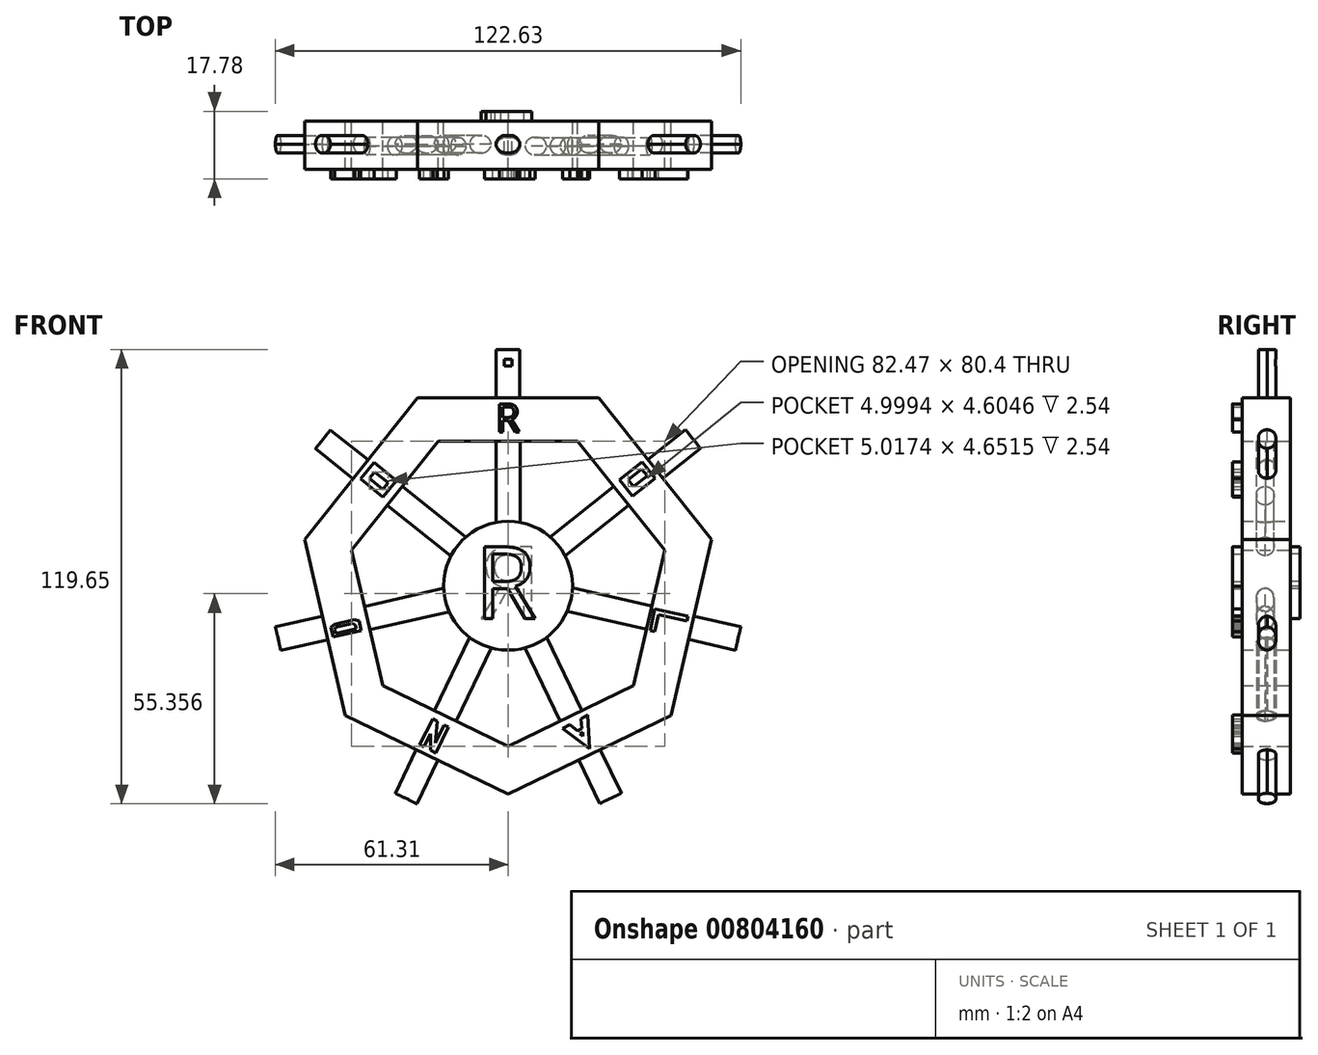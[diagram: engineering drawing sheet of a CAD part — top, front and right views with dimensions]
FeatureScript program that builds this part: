
annotation { "Feature Type Name" : "Feature", "Feature Type Description" : "" }
export const myFeature = defineFeature(function(context is Context, id is Id, definition is map)
    precondition{}
    {
        {
            var Q0;
            Q0=qCreatedBy(makeId("Front.planeOp"),FACE);
            var sketch = newSketch(context, id + "F0", { "sketchPlane" : qUnion([Q0])});
            skCircle(sketch, "E0.cCircle", {"center": v(0, 0) * mm, "radius": 49.5 * mm, "construction": true});
            skLineSegment(sketch, "E0.0", {"start": v(-23.84, 49.5) * mm, "end": v(23.84, 49.5) * mm});
            skLineSegment(sketch, "E0.1", {"start": v(23.84, 49.5) * mm, "end": v(53.56, 12.22) * mm});
            skLineSegment(sketch, "E0.2", {"start": v(53.56, 12.22) * mm, "end": v(42.95, -34.25) * mm});
            skLineSegment(sketch, "E0.3", {"start": v(42.95, -34.25) * mm, "end": v(0, -54.94) * mm});
            skLineSegment(sketch, "E0.4", {"start": v(0, -54.94) * mm, "end": v(-42.95, -34.25) * mm});
            skLineSegment(sketch, "E0.5", {"start": v(-42.95, -34.25) * mm, "end": v(-53.56, 12.22) * mm});
            skLineSegment(sketch, "E0.6", {"start": v(-53.56, 12.22) * mm, "end": v(-23.84, 49.5) * mm});
            skPoint(sketch, "E0.0.midPoint", {"position": v(0, 49.5) * mm});
            skCircle(sketch, "E1.cCircle", {"center": v(0, 0) * mm, "radius": 38.1 * mm, "construction": true});
            skLineSegment(sketch, "E1.0", {"start": v(-18.35, 38.1) * mm, "end": v(18.35, 38.1) * mm});
            skLineSegment(sketch, "E1.1", {"start": v(18.35, 38.1) * mm, "end": v(41.24, 9.41) * mm});
            skLineSegment(sketch, "E1.2", {"start": v(41.24, 9.41) * mm, "end": v(33.07, -26.37) * mm});
            skLineSegment(sketch, "E1.3", {"start": v(33.07, -26.37) * mm, "end": v(0, -42.3) * mm});
            skLineSegment(sketch, "E1.4", {"start": v(0, -42.3) * mm, "end": v(-33.07, -26.37) * mm});
            skLineSegment(sketch, "E1.5", {"start": v(-33.07, -26.37) * mm, "end": v(-41.24, 9.41) * mm});
            skLineSegment(sketch, "E1.6", {"start": v(-41.24, 9.41) * mm, "end": v(-18.35, 38.1) * mm});
            skPoint(sketch, "E1.0.midPoint", {"position": v(0, 38.1) * mm});
            skSolve(sketch);
        }
        {
            var Q0;
            Q0=makeQuery(id+"F0.imprint","IMPRINT",FACE,{"disambiguationData":[TD([[makeQuery(id+"F0.imprint","IMPRINT",EDGE,{"derivedFrom":sQuery(id+"F0.wireOp",EDGE,"E0.0")}),-1.0]])]});
            extrude(context, id + "F1", {"entities" : qUnion([Q0]), "depth" : 12.7 * mm, "offsetDistance" : 25.4 * mm});
        }
        {
            var Q0;
            Q0=makeQuery(id+"F1.opExtrude","SWEPT_FACE",FACE,{"disambiguationData":[OSD([sQuery(id+"F0.wireOp",EDGE,"E1.5")])]});
            var sketch = newSketch(context, id + "F2", { "sketchPlane" : qUnion([Q0])});
            skLineSegment(sketch, "E2.bottom", {"start": v(-4.32, 3.11) * mm, "end": v(-8.9, 3.11) * mm});
            skLineSegment(sketch, "E2.top", {"start": v(-4.32, -3.24) * mm, "end": v(-8.9, -3.24) * mm});
            skLineSegment(sketch, "E2.left", {"start": v(-4.32, 3.11) * mm, "end": v(-4.32, -3.24) * mm});
            skLineSegment(sketch, "E2.right", {"start": v(-8.9, 3.11) * mm, "end": v(-8.9, -3.24) * mm});
            skSolve(sketch);
        }
        {
            var Q0;
            Q0=makeQuery(id+"F1.opExtrude","SWEPT_FACE",FACE,{"disambiguationData":[OSD([sQuery(id+"F0.wireOp",EDGE,"E1.4")])]});
            var sketch = newSketch(context, id + "F3", { "sketchPlane" : qUnion([Q0])});
            skLineSegment(sketch, "E3.bottom", {"start": v(3.11, -8.38) * mm, "end": v(-3.24, -8.38) * mm});
            skLineSegment(sketch, "E3.top", {"start": v(3.11, -3.8) * mm, "end": v(-3.24, -3.81) * mm});
            skLineSegment(sketch, "E3.left", {"start": v(3.11, -8.38) * mm, "end": v(3.11, -3.8) * mm});
            skLineSegment(sketch, "E3.right", {"start": v(-3.24, -8.38) * mm, "end": v(-3.24, -3.81) * mm});
            skSolve(sketch);
        }
        {
            var Q0;
            Q0=makeQuery(id+"F1.opExtrude","SWEPT_FACE",FACE,{"disambiguationData":[OSD([sQuery(id+"F0.wireOp",EDGE,"E1.3")])]});
            var sketch = newSketch(context, id + "F4", { "sketchPlane" : qUnion([Q0])});
            skLineSegment(sketch, "E4.bottom", {"start": v(-3.11, -4.32) * mm, "end": v(3.24, -4.32) * mm});
            skLineSegment(sketch, "E4.top", {"start": v(-3.11, -8.9) * mm, "end": v(3.24, -8.9) * mm});
            skLineSegment(sketch, "E4.left", {"start": v(-3.11, -4.32) * mm, "end": v(-3.11, -8.9) * mm});
            skLineSegment(sketch, "E4.right", {"start": v(3.24, -4.32) * mm, "end": v(3.24, -8.9) * mm});
            skSolve(sketch);
        }
        {
            var Q0;
            Q0=makeQuery(id+"F1.opExtrude","SWEPT_FACE",FACE,{"disambiguationData":[OSD([sQuery(id+"F0.wireOp",EDGE,"E1.2")])]});
            var sketch = newSketch(context, id + "F5", { "sketchPlane" : qUnion([Q0])});
            skPoint(sketch, "E5.oppositeSnap0", {"position": v(0, 0) * mm});
            skLineSegment(sketch, "E6.bottom", {"start": v(4.32, -3.11) * mm, "end": v(8.9, -3.11) * mm});
            skLineSegment(sketch, "E6.top", {"start": v(4.32, 3.24) * mm, "end": v(8.9, 3.24) * mm});
            skLineSegment(sketch, "E6.left", {"start": v(4.32, -3.11) * mm, "end": v(4.32, 3.24) * mm});
            skLineSegment(sketch, "E6.right", {"start": v(8.9, -3.11) * mm, "end": v(8.9, 3.24) * mm});
            skSolve(sketch);
        }
        {
            var Q0;
            Q0=makeQuery(id+"F1.opExtrude","SWEPT_FACE",FACE,{"disambiguationData":[OSD([sQuery(id+"F0.wireOp",EDGE,"E1.1")])]});
            var sketch = newSketch(context, id + "F6", { "sketchPlane" : qUnion([Q0])});
            skLineSegment(sketch, "E7.bottom", {"start": v(4.32, -3.24) * mm, "end": v(8.9, -3.24) * mm});
            skLineSegment(sketch, "E7.top", {"start": v(4.32, 3.11) * mm, "end": v(8.9, 3.11) * mm});
            skLineSegment(sketch, "E7.left", {"start": v(4.32, -3.24) * mm, "end": v(4.32, 3.11) * mm});
            skLineSegment(sketch, "E7.right", {"start": v(8.9, -3.24) * mm, "end": v(8.9, 3.11) * mm});
            skSolve(sketch);
        }
        {
            var Q0;
            Q0=makeQuery(id+"F1.opExtrude","SWEPT_FACE",FACE,{"disambiguationData":[OSD([sQuery(id+"F0.wireOp",EDGE,"E1.0")])]});
            var sketch = newSketch(context, id + "F7", { "sketchPlane" : qUnion([Q0])});
            skLineSegment(sketch, "E8.bottom", {"start": v(3.24, 4.32) * mm, "end": v(-3.11, 4.32) * mm});
            skLineSegment(sketch, "E8.top", {"start": v(3.24, 8.9) * mm, "end": v(-3.11, 8.9) * mm});
            skLineSegment(sketch, "E8.left", {"start": v(3.24, 4.32) * mm, "end": v(3.24, 8.9) * mm});
            skLineSegment(sketch, "E8.right", {"start": v(-3.11, 4.32) * mm, "end": v(-3.11, 8.9) * mm});
            skSolve(sketch);
        }
        {
            var Q0;
            Q0=makeQuery(id+"F1.opExtrude","SWEPT_FACE",FACE,{"disambiguationData":[OSD([sQuery(id+"F0.wireOp",EDGE,"E1.6")])]});
            var sketch = newSketch(context, id + "F8", { "sketchPlane" : qUnion([Q0])});
            skLineSegment(sketch, "E9.bottom", {"start": v(-4.32, 3.11) * mm, "end": v(-8.9, 3.11) * mm});
            skLineSegment(sketch, "E9.top", {"start": v(-4.32, -3.24) * mm, "end": v(-8.89, -3.24) * mm});
            skLineSegment(sketch, "E9.left", {"start": v(-4.32, 3.11) * mm, "end": v(-4.32, -3.24) * mm});
            skLineSegment(sketch, "E9.right", {"start": v(-8.9, 3.11) * mm, "end": v(-8.89, -3.24) * mm});
            skSolve(sketch);
        }
        {
            var Q0;
            Q0=makeQuery(id+"F7.imprint","IMPRINT",FACE,{"disambiguationData":[TD([[makeQuery(id+"F7.imprint","IMPRINT",EDGE,{"derivedFrom":sQuery(id+"F7.wireOp",EDGE,"E8.bottom")}),-1.0]])]});
            extrude(context, id + "F9", {"entities" : qUnion([Q0]), "operationType" : NewBodyOperationType.ADD, "depth" : 25.4 * mm, "offsetDistance" : 25.4 * mm});
        }
        {
            var Q0;
            Q0=makeQuery(id+"F2.imprint","IMPRINT",FACE,{"disambiguationData":[TD([[makeQuery(id+"F2.imprint","IMPRINT",EDGE,{"derivedFrom":sQuery(id+"F2.wireOp",EDGE,"E2.bottom")}),1.0]])]});
            extrude(context, id + "F10", {"entities" : qUnion([Q0]), "operationType" : NewBodyOperationType.ADD, "depth" : 25.4 * mm, "offsetDistance" : 25.4 * mm});
        }
        {
            var Q0;
            Q0=makeQuery(id+"F4.imprint","IMPRINT",FACE,{"disambiguationData":[TD([[makeQuery(id+"F4.imprint","IMPRINT",EDGE,{"derivedFrom":sQuery(id+"F4.wireOp",EDGE,"E4.bottom")}),-1.0]])]});
            extrude(context, id + "F11", {"entities" : qUnion([Q0]), "operationType" : NewBodyOperationType.ADD, "depth" : 25.4 * mm, "offsetDistance" : 25.4 * mm});
        }
        {
            var Q0;
            Q0=makeQuery(id+"F6.imprint","IMPRINT",FACE,{"disambiguationData":[TD([[makeQuery(id+"F6.imprint","IMPRINT",EDGE,{"derivedFrom":sQuery(id+"F6.wireOp",EDGE,"E7.bottom")}),1.0]])]});
            extrude(context, id + "F12", {"entities" : qUnion([Q0]), "operationType" : NewBodyOperationType.ADD, "depth" : 25.4 * mm, "offsetDistance" : 25.4 * mm});
        }
        {
            var Q0;
            Q0=makeQuery(id+"F3.imprint","IMPRINT",FACE,{"disambiguationData":[TD([[makeQuery(id+"F3.imprint","IMPRINT",EDGE,{"derivedFrom":sQuery(id+"F3.wireOp",EDGE,"E3.bottom")}),-1.0]])]});
            extrude(context, id + "F13", {"entities" : qUnion([Q0]), "operationType" : NewBodyOperationType.ADD, "depth" : 25.4 * mm, "offsetDistance" : 25.4 * mm});
        }
        {
            var Q0;
            Q0=makeQuery(id+"F5.imprint","IMPRINT",FACE,{"disambiguationData":[TD([[makeQuery(id+"F5.imprint","IMPRINT",EDGE,{"derivedFrom":sQuery(id+"F5.wireOp",EDGE,"E6.bottom")}),1.0]])]});
            extrude(context, id + "F14", {"entities" : qUnion([Q0]), "operationType" : NewBodyOperationType.ADD, "depth" : 25.4 * mm, "offsetDistance" : 25.4 * mm});
        }
        {
            var Q0;
            Q0=makeQuery(id+"F8.imprint","IMPRINT",FACE,{"disambiguationData":[TD([[makeQuery(id+"F8.imprint","IMPRINT",EDGE,{"derivedFrom":sQuery(id+"F8.wireOp",EDGE,"E9.bottom")}),1.0]])]});
            extrude(context, id + "F15", {"entities" : qUnion([Q0]), "operationType" : NewBodyOperationType.ADD, "depth" : 25.4 * mm, "offsetDistance" : 25.4 * mm});
        }
        {
            var Q0;
            Q0=qCreatedBy(makeId("Front.planeOp"),FACE);
            var sketch = newSketch(context, id + "F16", { "sketchPlane" : qUnion([Q0])});
            skCircle(sketch, "E10", {"center": v(0, 0) * mm, "radius": 16.97 * mm});
            skSolve(sketch);
        }
        {
            var Q0;
            Q0=makeQuery(id+"F16.imprint","IMPRINT",FACE,{"disambiguationData":[TD([[makeQuery(id+"F16.imprint","IMPRINT",EDGE,{"derivedFrom":sQuery(id+"F16.wireOp",EDGE,"E10")}),1.0]])]});
            extrude(context, id + "F17", {"entities" : qUnion([Q0]), "operationType" : NewBodyOperationType.ADD, "depth" : 12.7 * mm, "offsetDistance" : 25.4 * mm});
        }
        {
            var Q0;
            Q0=makeQuery(id+"F14.opExtrude","SWEPT_EDGE",EDGE,{"disambiguationData":[OSD([sQuery(id+"F5.wireOp",EDGE,"E6.top"),sQuery(id+"F5.wireOp",EDGE,"E6.right")])]});
            var Q1;
            Q1=makeQuery(id+"F14.opExtrude","SWEPT_EDGE",EDGE,{"disambiguationData":[OSD([sQuery(id+"F5.wireOp",EDGE,"E6.bottom"),sQuery(id+"F5.wireOp",EDGE,"E6.left")])]});
            var Q2;
            Q2=makeQuery(id+"F14.opExtrude","SWEPT_EDGE",EDGE,{"disambiguationData":[OSD([sQuery(id+"F5.wireOp",EDGE,"E6.bottom"),sQuery(id+"F5.wireOp",EDGE,"E6.right")])]});
            var Q3;
            Q3=makeQuery(id+"F14.opExtrude","SWEPT_EDGE",EDGE,{"disambiguationData":[OSD([sQuery(id+"F5.wireOp",EDGE,"E6.top"),sQuery(id+"F5.wireOp",EDGE,"E6.left")])]});
            fillet(context, id + "F18", {"entities" : qUnion([Q0, Q1, Q2, Q3]), "radius" : 2.54 * mm, "tangentPropagation" : true, "allowEdgeOverflow" : false});
        }
        {
            var Q0;
            Q0=makeQuery(id+"F12.opExtrude","SWEPT_EDGE",EDGE,{"disambiguationData":[OSD([sQuery(id+"F6.wireOp",EDGE,"E7.top"),sQuery(id+"F6.wireOp",EDGE,"E7.right")])]});
            var Q1;
            Q1=makeQuery(id+"F12.opExtrude","SWEPT_EDGE",EDGE,{"disambiguationData":[OSD([sQuery(id+"F6.wireOp",EDGE,"E7.bottom"),sQuery(id+"F6.wireOp",EDGE,"E7.right")])]});
            var Q2;
            Q2=makeQuery(id+"F12.opExtrude","SWEPT_EDGE",EDGE,{"disambiguationData":[OSD([sQuery(id+"F6.wireOp",EDGE,"E7.bottom"),sQuery(id+"F6.wireOp",EDGE,"E7.left")])]});
            var Q3;
            Q3=makeQuery(id+"F12.opExtrude","SWEPT_EDGE",EDGE,{"disambiguationData":[OSD([sQuery(id+"F6.wireOp",EDGE,"E7.top"),sQuery(id+"F6.wireOp",EDGE,"E7.left")])]});
            fillet(context, id + "F19", {"entities" : qUnion([Q0, Q1, Q2, Q3]), "radius" : 2.54 * mm, "tangentPropagation" : true, "allowEdgeOverflow" : false});
        }
        {
            var Q0;
            Q0=makeQuery(id+"F9.opExtrude","SWEPT_EDGE",EDGE,{"disambiguationData":[OSD([sQuery(id+"F7.wireOp",EDGE,"E8.top"),sQuery(id+"F7.wireOp",EDGE,"E8.right")])]});
            var Q1;
            Q1=makeQuery(id+"F9.opExtrude","SWEPT_EDGE",EDGE,{"disambiguationData":[OSD([sQuery(id+"F7.wireOp",EDGE,"E8.bottom"),sQuery(id+"F7.wireOp",EDGE,"E8.left")])]});
            var Q2;
            Q2=makeQuery(id+"F9.opExtrude","SWEPT_EDGE",EDGE,{"disambiguationData":[OSD([sQuery(id+"F7.wireOp",EDGE,"E8.top"),sQuery(id+"F7.wireOp",EDGE,"E8.left")])]});
            var Q3;
            Q3=makeQuery(id+"F9.opExtrude","SWEPT_EDGE",EDGE,{"disambiguationData":[OSD([sQuery(id+"F7.wireOp",EDGE,"E8.bottom"),sQuery(id+"F7.wireOp",EDGE,"E8.right")])]});
            fillet(context, id + "F20", {"entities" : qUnion([Q0, Q1, Q2, Q3]), "radius" : 2.54 * mm, "tangentPropagation" : true, "allowEdgeOverflow" : false});
        }
        {
            var Q0;
            Q0=makeQuery(id+"F15.opExtrude","SWEPT_EDGE",EDGE,{"disambiguationData":[OSD([sQuery(id+"F8.wireOp",EDGE,"E9.top"),sQuery(id+"F8.wireOp",EDGE,"E9.left")])]});
            var Q1;
            Q1=makeQuery(id+"F15.opExtrude","SWEPT_EDGE",EDGE,{"disambiguationData":[OSD([sQuery(id+"F8.wireOp",EDGE,"E9.bottom"),sQuery(id+"F8.wireOp",EDGE,"E9.left")])]});
            var Q2;
            Q2=makeQuery(id+"F15.opExtrude","SWEPT_EDGE",EDGE,{"disambiguationData":[OSD([sQuery(id+"F8.wireOp",EDGE,"E9.top"),sQuery(id+"F8.wireOp",EDGE,"E9.right")])]});
            var Q3;
            Q3=makeQuery(id+"F15.opExtrude","SWEPT_EDGE",EDGE,{"disambiguationData":[OSD([sQuery(id+"F8.wireOp",EDGE,"E9.bottom"),sQuery(id+"F8.wireOp",EDGE,"E9.right")])]});
            fillet(context, id + "F21", {"entities" : qUnion([Q0, Q1, Q2, Q3]), "radius" : 2.54 * mm, "tangentPropagation" : true, "allowEdgeOverflow" : false});
        }
        {
            var Q0;
            Q0=makeQuery(id+"F10.opExtrude","SWEPT_EDGE",EDGE,{"disambiguationData":[OSD([sQuery(id+"F2.wireOp",EDGE,"E2.top"),sQuery(id+"F2.wireOp",EDGE,"E2.left")])]});
            var Q1;
            Q1=makeQuery(id+"F10.opExtrude","SWEPT_EDGE",EDGE,{"disambiguationData":[OSD([sQuery(id+"F2.wireOp",EDGE,"E2.bottom"),sQuery(id+"F2.wireOp",EDGE,"E2.left")])]});
            var Q2;
            Q2=makeQuery(id+"F10.opExtrude","SWEPT_EDGE",EDGE,{"disambiguationData":[OSD([sQuery(id+"F2.wireOp",EDGE,"E2.bottom"),sQuery(id+"F2.wireOp",EDGE,"E2.right")])]});
            var Q3;
            Q3=makeQuery(id+"F10.opExtrude","SWEPT_EDGE",EDGE,{"disambiguationData":[OSD([sQuery(id+"F2.wireOp",EDGE,"E2.top"),sQuery(id+"F2.wireOp",EDGE,"E2.right")])]});
            fillet(context, id + "F22", {"entities" : qUnion([Q0, Q1, Q2, Q3]), "radius" : 2.54 * mm, "tangentPropagation" : true, "allowEdgeOverflow" : false});
        }
        {
            var Q0;
            Q0=makeQuery(id+"F13.opExtrude","SWEPT_EDGE",EDGE,{"disambiguationData":[OSD([sQuery(id+"F3.wireOp",EDGE,"E3.top"),sQuery(id+"F3.wireOp",EDGE,"E3.right")])]});
            var Q1;
            Q1=makeQuery(id+"F13.opExtrude","SWEPT_EDGE",EDGE,{"disambiguationData":[OSD([sQuery(id+"F3.wireOp",EDGE,"E3.top"),sQuery(id+"F3.wireOp",EDGE,"E3.left")])]});
            var Q2;
            Q2=makeQuery(id+"F13.opExtrude","SWEPT_EDGE",EDGE,{"disambiguationData":[OSD([sQuery(id+"F3.wireOp",EDGE,"E3.bottom"),sQuery(id+"F3.wireOp",EDGE,"E3.left")])]});
            var Q3;
            Q3=makeQuery(id+"F13.opExtrude","SWEPT_EDGE",EDGE,{"disambiguationData":[OSD([sQuery(id+"F3.wireOp",EDGE,"E3.bottom"),sQuery(id+"F3.wireOp",EDGE,"E3.right")])]});
            fillet(context, id + "F23", {"entities" : qUnion([Q0, Q1, Q2, Q3]), "radius" : 2.54 * mm, "tangentPropagation" : true, "allowEdgeOverflow" : false});
        }
        {
            var Q0;
            Q0=makeQuery(id+"F11.opExtrude","SWEPT_EDGE",EDGE,{"disambiguationData":[OSD([sQuery(id+"F4.wireOp",EDGE,"E4.bottom"),sQuery(id+"F4.wireOp",EDGE,"E4.right")])]});
            var Q1;
            Q1=makeQuery(id+"F11.opExtrude","SWEPT_EDGE",EDGE,{"disambiguationData":[OSD([sQuery(id+"F4.wireOp",EDGE,"E4.bottom"),sQuery(id+"F4.wireOp",EDGE,"E4.left")])]});
            var Q2;
            Q2=makeQuery(id+"F11.opExtrude","SWEPT_EDGE",EDGE,{"disambiguationData":[OSD([sQuery(id+"F4.wireOp",EDGE,"E4.top"),sQuery(id+"F4.wireOp",EDGE,"E4.right")])]});
            var Q3;
            Q3=makeQuery(id+"F11.opExtrude","SWEPT_EDGE",EDGE,{"disambiguationData":[OSD([sQuery(id+"F4.wireOp",EDGE,"E4.top"),sQuery(id+"F4.wireOp",EDGE,"E4.left")])]});
            fillet(context, id + "F24", {"entities" : qUnion([Q0, Q1, Q2, Q3]), "radius" : 2.54 * mm, "tangentPropagation" : true, "allowEdgeOverflow" : false});
        }
        {
            var Q0;
            Q0=makeQuery(id+"F1.opExtrude","SWEPT_FACE",FACE,{"disambiguationData":[OSD([sQuery(id+"F0.wireOp",EDGE,"E0.5")])]});
            var sketch = newSketch(context, id + "F25", { "sketchPlane" : qUnion([Q0])});
            skLineSegment(sketch, "E11.bottom", {"start": v(3.81, -3.3) * mm, "end": v(8.38, -3.3) * mm});
            skLineSegment(sketch, "E11.top", {"start": v(3.8, 3.05) * mm, "end": v(8.38, 3.05) * mm});
            skLineSegment(sketch, "E11.left", {"start": v(3.81, -3.3) * mm, "end": v(3.8, 3.05) * mm});
            skLineSegment(sketch, "E11.right", {"start": v(8.38, -3.3) * mm, "end": v(8.38, 3.05) * mm});
            skSolve(sketch);
        }
        {
            var Q0;
            Q0=makeQuery(id+"F25.imprint","IMPRINT",FACE,{"disambiguationData":[TD([[makeQuery(id+"F25.imprint","IMPRINT",EDGE,{"derivedFrom":sQuery(id+"F25.wireOp",EDGE,"E11.bottom")}),1.0]])]});
            extrude(context, id + "F26", {"entities" : qUnion([Q0]), "operationType" : NewBodyOperationType.ADD, "depth" : 12.7 * mm, "offsetDistance" : 25.4 * mm});
        }
        {
            var Q0;
            Q0=makeQuery(id+"F1.opExtrude","SWEPT_FACE",FACE,{"disambiguationData":[OSD([sQuery(id+"F0.wireOp",EDGE,"E0.4")])]});
            var sketch = newSketch(context, id + "F27", { "sketchPlane" : qUnion([Q0])});
            skLineSegment(sketch, "E12.bottom", {"start": v(-3.08, 8.38) * mm, "end": v(3.27, 8.38) * mm});
            skLineSegment(sketch, "E12.top", {"start": v(-3.08, 3.81) * mm, "end": v(3.27, 3.81) * mm});
            skLineSegment(sketch, "E12.left", {"start": v(-3.08, 8.38) * mm, "end": v(-3.08, 3.81) * mm});
            skLineSegment(sketch, "E12.right", {"start": v(3.27, 8.38) * mm, "end": v(3.27, 3.81) * mm});
            skSolve(sketch);
        }
        {
            var Q0;
            Q0=makeQuery(id+"F1.opExtrude","SWEPT_FACE",FACE,{"disambiguationData":[OSD([sQuery(id+"F0.wireOp",EDGE,"E0.3")])]});
            var sketch = newSketch(context, id + "F28", { "sketchPlane" : qUnion([Q0])});
            skLineSegment(sketch, "E13.bottom", {"start": v(-3.17, 8.38) * mm, "end": v(3.18, 8.38) * mm});
            skLineSegment(sketch, "E13.top", {"start": v(-3.17, 3.8) * mm, "end": v(3.18, 3.8) * mm});
            skLineSegment(sketch, "E13.left", {"start": v(-3.17, 8.38) * mm, "end": v(-3.17, 3.8) * mm});
            skLineSegment(sketch, "E13.right", {"start": v(3.18, 8.38) * mm, "end": v(3.18, 3.8) * mm});
            skSolve(sketch);
        }
        {
            var Q0;
            Q0=makeQuery(id+"F1.opExtrude","SWEPT_FACE",FACE,{"disambiguationData":[OSD([sQuery(id+"F0.wireOp",EDGE,"E0.2")])]});
            var sketch = newSketch(context, id + "F29", { "sketchPlane" : qUnion([Q0])});
            skLineSegment(sketch, "E14.bottom", {"start": v(-8.38, -3.25) * mm, "end": v(-3.8, -3.25) * mm});
            skLineSegment(sketch, "E14.top", {"start": v(-8.38, 3.1) * mm, "end": v(-3.81, 3.1) * mm});
            skLineSegment(sketch, "E14.left", {"start": v(-8.38, -3.25) * mm, "end": v(-8.38, 3.1) * mm});
            skLineSegment(sketch, "E14.right", {"start": v(-3.8, -3.25) * mm, "end": v(-3.81, 3.1) * mm});
            skSolve(sketch);
        }
        {
            var Q0;
            Q0=makeQuery(id+"F1.opExtrude","SWEPT_FACE",FACE,{"disambiguationData":[OSD([sQuery(id+"F0.wireOp",EDGE,"E0.1")])]});
            var sketch = newSketch(context, id + "F30", { "sketchPlane" : qUnion([Q0])});
            skLineSegment(sketch, "E15.bottom", {"start": v(-8.38, -3.34) * mm, "end": v(-3.8, -3.34) * mm});
            skLineSegment(sketch, "E15.top", {"start": v(-8.38, 3) * mm, "end": v(-3.81, 3) * mm});
            skLineSegment(sketch, "E15.left", {"start": v(-8.38, -3.34) * mm, "end": v(-8.38, 3) * mm});
            skLineSegment(sketch, "E15.right", {"start": v(-3.8, -3.34) * mm, "end": v(-3.81, 3) * mm});
            skSolve(sketch);
        }
        {
            var Q0;
            Q0=makeQuery(id+"F1.opExtrude","SWEPT_FACE",FACE,{"disambiguationData":[OSD([sQuery(id+"F0.wireOp",EDGE,"E0.0")])]});
            var sketch = newSketch(context, id + "F31", { "sketchPlane" : qUnion([Q0])});
            skLineSegment(sketch, "E16.bottom", {"start": v(3.14, -8.38) * mm, "end": v(-3.21, -8.38) * mm});
            skLineSegment(sketch, "E16.top", {"start": v(3.14, -3.8) * mm, "end": v(-3.21, -3.81) * mm});
            skLineSegment(sketch, "E16.left", {"start": v(3.14, -8.38) * mm, "end": v(3.14, -3.81) * mm});
            skLineSegment(sketch, "E16.right", {"start": v(-3.21, -8.38) * mm, "end": v(-3.21, -3.81) * mm});
            skSolve(sketch);
        }
        {
            var Q0;
            Q0=makeQuery(id+"F1.opExtrude","SWEPT_FACE",FACE,{"disambiguationData":[OSD([sQuery(id+"F0.wireOp",EDGE,"E0.6")])]});
            var sketch = newSketch(context, id + "F32", { "sketchPlane" : qUnion([Q0])});
            skLineSegment(sketch, "E17.bottom", {"start": v(8.38, 2.93) * mm, "end": v(3.8, 2.93) * mm});
            skLineSegment(sketch, "E17.top", {"start": v(8.38, -3.42) * mm, "end": v(3.81, -3.42) * mm});
            skLineSegment(sketch, "E17.left", {"start": v(8.38, 2.93) * mm, "end": v(8.38, -3.42) * mm});
            skLineSegment(sketch, "E17.right", {"start": v(3.8, 2.93) * mm, "end": v(3.81, -3.42) * mm});
            skSolve(sketch);
        }
        {
            var Q0;
            Q0=makeQuery(id+"F32.imprint","IMPRINT",FACE,{"disambiguationData":[TD([[makeQuery(id+"F32.imprint","IMPRINT",EDGE,{"derivedFrom":sQuery(id+"F32.wireOp",EDGE,"E17.bottom")}),1.0]])]});
            extrude(context, id + "F33", {"entities" : qUnion([Q0]), "operationType" : NewBodyOperationType.ADD, "depth" : 12.7 * mm, "offsetDistance" : 25.4 * mm});
        }
        {
            var Q0;
            Q0=makeQuery(id+"F31.imprint","IMPRINT",FACE,{"disambiguationData":[TD([[makeQuery(id+"F31.imprint","IMPRINT",EDGE,{"derivedFrom":sQuery(id+"F31.wireOp",EDGE,"E16.bottom")}),-1.0]])]});
            extrude(context, id + "F34", {"entities" : qUnion([Q0]), "operationType" : NewBodyOperationType.ADD, "depth" : 12.7 * mm, "offsetDistance" : 25.4 * mm});
        }
        {
            var Q0;
            Q0=makeQuery(id+"F30.imprint","IMPRINT",FACE,{"disambiguationData":[TD([[makeQuery(id+"F30.imprint","IMPRINT",EDGE,{"derivedFrom":sQuery(id+"F30.wireOp",EDGE,"E15.bottom")}),1.0]])]});
            extrude(context, id + "F35", {"entities" : qUnion([Q0]), "operationType" : NewBodyOperationType.ADD, "depth" : 12.7 * mm, "offsetDistance" : 25.4 * mm});
        }
        {
            var Q0;
            Q0=makeQuery(id+"F29.imprint","IMPRINT",FACE,{"disambiguationData":[TD([[makeQuery(id+"F29.imprint","IMPRINT",EDGE,{"derivedFrom":sQuery(id+"F29.wireOp",EDGE,"E14.bottom")}),1.0]])]});
            extrude(context, id + "F36", {"entities" : qUnion([Q0]), "operationType" : NewBodyOperationType.ADD, "depth" : 12.7 * mm, "offsetDistance" : 25.4 * mm});
        }
        {
            var Q0;
            Q0=makeQuery(id+"F28.imprint","IMPRINT",FACE,{"disambiguationData":[TD([[makeQuery(id+"F28.imprint","IMPRINT",EDGE,{"derivedFrom":sQuery(id+"F28.wireOp",EDGE,"E13.bottom")}),-1.0]])]});
            extrude(context, id + "F37", {"entities" : qUnion([Q0]), "operationType" : NewBodyOperationType.ADD, "depth" : 12.7 * mm, "offsetDistance" : 25.4 * mm});
        }
        {
            var Q0;
            Q0=makeQuery(id+"F27.imprint","IMPRINT",FACE,{"disambiguationData":[TD([[makeQuery(id+"F27.imprint","IMPRINT",EDGE,{"derivedFrom":sQuery(id+"F27.wireOp",EDGE,"E12.bottom")}),-1.0]])]});
            extrude(context, id + "F38", {"entities" : qUnion([Q0]), "operationType" : NewBodyOperationType.ADD, "depth" : 12.7 * mm, "offsetDistance" : 25.4 * mm});
        }
        {
            var Q0;
            Q0=makeQuery(id+"F26.opExtrude","SWEPT_EDGE",EDGE,{"disambiguationData":[OSD([sQuery(id+"F25.wireOp",EDGE,"E11.bottom"),sQuery(id+"F25.wireOp",EDGE,"E11.right")])]});
            var Q1;
            Q1=makeQuery(id+"F26.opExtrude","SWEPT_EDGE",EDGE,{"disambiguationData":[OSD([sQuery(id+"F25.wireOp",EDGE,"E11.top"),sQuery(id+"F25.wireOp",EDGE,"E11.right")])]});
            var Q2;
            Q2=makeQuery(id+"F26.opExtrude","SWEPT_EDGE",EDGE,{"disambiguationData":[OSD([sQuery(id+"F25.wireOp",EDGE,"E11.top"),sQuery(id+"F25.wireOp",EDGE,"E11.left")])]});
            var Q3;
            Q3=makeQuery(id+"F26.opExtrude","SWEPT_EDGE",EDGE,{"disambiguationData":[OSD([sQuery(id+"F25.wireOp",EDGE,"E11.bottom"),sQuery(id+"F25.wireOp",EDGE,"E11.left")])]});
            fillet(context, id + "F39", {"entities" : qUnion([Q0, Q1, Q2, Q3]), "radius" : 2.54 * mm, "tangentPropagation" : true, "allowEdgeOverflow" : false});
        }
        {
            var Q0;
            Q0=makeQuery(id+"F38.opExtrude","SWEPT_EDGE",EDGE,{"disambiguationData":[OSD([sQuery(id+"F27.wireOp",EDGE,"E12.bottom"),sQuery(id+"F27.wireOp",EDGE,"E12.right")])]});
            var Q1;
            Q1=makeQuery(id+"F38.opExtrude","SWEPT_EDGE",EDGE,{"disambiguationData":[OSD([sQuery(id+"F27.wireOp",EDGE,"E12.bottom"),sQuery(id+"F27.wireOp",EDGE,"E12.left")])]});
            var Q2;
            Q2=makeQuery(id+"F38.opExtrude","SWEPT_EDGE",EDGE,{"disambiguationData":[OSD([sQuery(id+"F27.wireOp",EDGE,"E12.top"),sQuery(id+"F27.wireOp",EDGE,"E12.right")])]});
            var Q3;
            Q3=makeQuery(id+"F38.opExtrude","SWEPT_EDGE",EDGE,{"disambiguationData":[OSD([sQuery(id+"F27.wireOp",EDGE,"E12.top"),sQuery(id+"F27.wireOp",EDGE,"E12.left")])]});
            fillet(context, id + "F40", {"entities" : qUnion([Q0, Q1, Q2, Q3]), "radius" : 2.54 * mm, "tangentPropagation" : true, "allowEdgeOverflow" : false});
        }
        {
            var Q0;
            Q0=makeQuery(id+"F37.opExtrude","SWEPT_EDGE",EDGE,{"disambiguationData":[OSD([sQuery(id+"F28.wireOp",EDGE,"E13.bottom"),sQuery(id+"F28.wireOp",EDGE,"E13.left")])]});
            var Q1;
            Q1=makeQuery(id+"F37.opExtrude","SWEPT_EDGE",EDGE,{"disambiguationData":[OSD([sQuery(id+"F28.wireOp",EDGE,"E13.bottom"),sQuery(id+"F28.wireOp",EDGE,"E13.right")])]});
            var Q2;
            Q2=makeQuery(id+"F37.opExtrude","SWEPT_EDGE",EDGE,{"disambiguationData":[OSD([sQuery(id+"F28.wireOp",EDGE,"E13.top"),sQuery(id+"F28.wireOp",EDGE,"E13.left")])]});
            var Q3;
            Q3=makeQuery(id+"F37.opExtrude","SWEPT_EDGE",EDGE,{"disambiguationData":[OSD([sQuery(id+"F28.wireOp",EDGE,"E13.top"),sQuery(id+"F28.wireOp",EDGE,"E13.right")])]});
            fillet(context, id + "F41", {"entities" : qUnion([Q0, Q1, Q2, Q3]), "radius" : 2.54 * mm, "tangentPropagation" : true, "allowEdgeOverflow" : false});
        }
        {
            var Q0;
            Q0=makeQuery(id+"F36.opExtrude","SWEPT_EDGE",EDGE,{"disambiguationData":[OSD([sQuery(id+"F29.wireOp",EDGE,"E14.top"),sQuery(id+"F29.wireOp",EDGE,"E14.left")])]});
            var Q1;
            Q1=makeQuery(id+"F36.opExtrude","SWEPT_EDGE",EDGE,{"disambiguationData":[OSD([sQuery(id+"F29.wireOp",EDGE,"E14.bottom"),sQuery(id+"F29.wireOp",EDGE,"E14.left")])]});
            var Q2;
            Q2=makeQuery(id+"F36.opExtrude","SWEPT_EDGE",EDGE,{"disambiguationData":[OSD([sQuery(id+"F29.wireOp",EDGE,"E14.bottom"),sQuery(id+"F29.wireOp",EDGE,"E14.right")])]});
            var Q3;
            Q3=makeQuery(id+"F36.opExtrude","SWEPT_EDGE",EDGE,{"disambiguationData":[OSD([sQuery(id+"F29.wireOp",EDGE,"E14.top"),sQuery(id+"F29.wireOp",EDGE,"E14.right")])]});
            fillet(context, id + "F42", {"entities" : qUnion([Q0, Q1, Q2, Q3]), "radius" : 2.54 * mm, "tangentPropagation" : true, "allowEdgeOverflow" : false});
        }
        {
            var Q0;
            Q0=makeQuery(id+"F35.opExtrude","SWEPT_EDGE",EDGE,{"disambiguationData":[OSD([sQuery(id+"F30.wireOp",EDGE,"E15.bottom"),sQuery(id+"F30.wireOp",EDGE,"E15.right")])]});
            var Q1;
            Q1=makeQuery(id+"F35.opExtrude","SWEPT_EDGE",EDGE,{"disambiguationData":[OSD([sQuery(id+"F30.wireOp",EDGE,"E15.top"),sQuery(id+"F30.wireOp",EDGE,"E15.right")])]});
            var Q2;
            Q2=makeQuery(id+"F35.opExtrude","SWEPT_EDGE",EDGE,{"disambiguationData":[OSD([sQuery(id+"F30.wireOp",EDGE,"E15.top"),sQuery(id+"F30.wireOp",EDGE,"E15.left")])]});
            var Q3;
            Q3=makeQuery(id+"F35.opExtrude","SWEPT_EDGE",EDGE,{"disambiguationData":[OSD([sQuery(id+"F30.wireOp",EDGE,"E15.bottom"),sQuery(id+"F30.wireOp",EDGE,"E15.left")])]});
            fillet(context, id + "F43", {"entities" : qUnion([Q0, Q1, Q2, Q3]), "radius" : 2.54 * mm, "tangentPropagation" : true, "allowEdgeOverflow" : false});
        }
        {
            var Q0;
            Q0=makeQuery(id+"F33.opExtrude","SWEPT_EDGE",EDGE,{"disambiguationData":[OSD([sQuery(id+"F32.wireOp",EDGE,"E17.top"),sQuery(id+"F32.wireOp",EDGE,"E17.left")])]});
            var Q1;
            Q1=makeQuery(id+"F33.opExtrude","SWEPT_EDGE",EDGE,{"disambiguationData":[OSD([sQuery(id+"F32.wireOp",EDGE,"E17.bottom"),sQuery(id+"F32.wireOp",EDGE,"E17.left")])]});
            var Q2;
            Q2=makeQuery(id+"F33.opExtrude","SWEPT_EDGE",EDGE,{"disambiguationData":[OSD([sQuery(id+"F32.wireOp",EDGE,"E17.bottom"),sQuery(id+"F32.wireOp",EDGE,"E17.right")])]});
            var Q3;
            Q3=makeQuery(id+"F33.opExtrude","SWEPT_EDGE",EDGE,{"disambiguationData":[OSD([sQuery(id+"F32.wireOp",EDGE,"E17.top"),sQuery(id+"F32.wireOp",EDGE,"E17.right")])]});
            fillet(context, id + "F44", {"entities" : qUnion([Q0, Q1, Q2, Q3]), "radius" : 2.54 * mm, "tangentPropagation" : true, "allowEdgeOverflow" : false});
        }
        {
            var Q0;
            Q0=makeQuery(id+"F34.opExtrude","SWEPT_EDGE",EDGE,{"disambiguationData":[OSD([sQuery(id+"F31.wireOp",EDGE,"E16.top"),sQuery(id+"F31.wireOp",EDGE,"E16.left")])]});
            var Q1;
            Q1=makeQuery(id+"F34.opExtrude","SWEPT_EDGE",EDGE,{"disambiguationData":[OSD([sQuery(id+"F31.wireOp",EDGE,"E16.top"),sQuery(id+"F31.wireOp",EDGE,"E16.right")])]});
            var Q2;
            Q2=makeQuery(id+"F34.opExtrude","SWEPT_EDGE",EDGE,{"disambiguationData":[OSD([sQuery(id+"F31.wireOp",EDGE,"E16.bottom"),sQuery(id+"F31.wireOp",EDGE,"E16.right")])]});
            var Q3;
            Q3=makeQuery(id+"F34.opExtrude","SWEPT_EDGE",EDGE,{"disambiguationData":[OSD([sQuery(id+"F31.wireOp",EDGE,"E16.bottom"),sQuery(id+"F31.wireOp",EDGE,"E16.left")])]});
            fillet(context, id + "F45", {"entities" : qUnion([Q0, Q1, Q2, Q3]), "radius" : 2.54 * mm, "tangentPropagation" : true, "allowEdgeOverflow" : false});
        }
        {
            var Q0;
            Q0=makeQuery(id+"F34.opExtrude","SWEPT_FACE",FACE,{"disambiguationData":[OSD([sQuery(id+"F31.wireOp",EDGE,"E16.top")])]});
            var sketch = newSketch(context, id + "F46", { "sketchPlane" : qUnion([Q0])});
            skLineSegment(sketch, "E18.bottom", {"start": v(-0.98, 59.71) * mm, "end": v(1.05, 59.71) * mm});
            skLineSegment(sketch, "E18.top", {"start": v(-0.98, 57.94) * mm, "end": v(1.05, 57.94) * mm});
            skLineSegment(sketch, "E18.left", {"start": v(-0.98, 59.71) * mm, "end": v(-0.98, 57.94) * mm});
            skLineSegment(sketch, "E18.right", {"start": v(1.05, 59.71) * mm, "end": v(1.05, 57.94) * mm});
            skSolve(sketch);
        }
        {
            var Q0;
            Q0=makeQuery(id+"F46.imprint","IMPRINT",FACE,{"disambiguationData":[TD([[makeQuery(id+"F46.imprint","IMPRINT",EDGE,{"derivedFrom":sQuery(id+"F46.wireOp",EDGE,"E18.bottom")}),-1.0]])]});
            extrude(context, id + "F47", {"entities" : qUnion([Q0]), "operationType" : NewBodyOperationType.REMOVE, "oppositeDirection" : true, "depth" : 25.4 * mm, "offsetDistance" : 25.4 * mm});
        }
        {
            var Q0;
            Q0=makeQuery(id+"F17.opExtrude","CAP_FACE",FACE,{"disambiguationData":[OSD([sQuery(id+"F16.wireOp",EDGE,"E10")])],"isStart":false});
            var sketch = newSketch(context, id + "F48", { "sketchPlane" : qUnion([Q0])});
            skText(sketch, "E19", { "text": "R", "fontName": "OpenSans-Regular.ttf"});
            const initialGuessF48  = {"E19": [-0.00884, -0.0087, 1, 0, 0.01912]};
            skSetInitialGuess(sketch, initialGuessF48);
            skSolve(sketch);
        }
        {
            var Q0;
            Q0=makeQuery(id+"F48.imprint","IMPRINT",FACE,{"disambiguationData":[TD([[makeQuery(id+"F48.imprint","IMPRINT",EDGE,{"derivedFrom":sQuery(id+"F48.wireOp",EDGE,"E19.sketch_text.stroke-0")}),-1.0]])]});
            extrude(context, id + "F49", {"entities" : qUnion([Q0]), "operationType" : NewBodyOperationType.ADD, "depth" : 2.54 * mm, "offsetDistance" : 25.4 * mm});
        }
        {
            var Q0;
            Q0=makeQuery(id+"F17.opExtrude","CAP_FACE",FACE,{"disambiguationData":[OSD([sQuery(id+"F16.wireOp",EDGE,"E10")])],"isStart":true});
            var sketch = newSketch(context, id + "F50", { "sketchPlane" : qUnion([Q0])});
            skText(sketch, "E20", { "text": "R\n", "fontName": "OpenSans-Regular.ttf"});
            const initialGuessF50  = {"E20": [-0.00884, -0.0087, 1, 0, 0.01911]};
            skSetInitialGuess(sketch, initialGuessF50);
            skSolve(sketch);
        }
        {
            var Q0;
            Q0=makeQuery(id+"F50.imprint","IMPRINT",FACE,{"disambiguationData":[TD([[makeQuery(id+"F50.imprint","IMPRINT",EDGE,{"derivedFrom":sQuery(id+"F50.wireOp",EDGE,"E20.sketch_text.stroke-0")}),-1.0]])]});
            extrude(context, id + "F51", {"entities" : qUnion([Q0]), "operationType" : NewBodyOperationType.ADD, "depth" : 2.54 * mm, "offsetDistance" : 25.4 * mm});
        }
        {
            var Q0;
            Q0=makeQuery(id+"F1.opExtrude","CAP_FACE",FACE,{"disambiguationData":[OSD([sQuery(id+"F0.wireOp",EDGE,"E0.0"),sQuery(id+"F0.wireOp",EDGE,"E0.1"),sQuery(id+"F0.wireOp",EDGE,"E0.2"),sQuery(id+"F0.wireOp",EDGE,"E0.3"),sQuery(id+"F0.wireOp",EDGE,"E0.4"),sQuery(id+"F0.wireOp",EDGE,"E0.5"),sQuery(id+"F0.wireOp",EDGE,"E0.6"),sQuery(id+"F0.wireOp",EDGE,"E1.0"),sQuery(id+"F0.wireOp",EDGE,"E1.1"),sQuery(id+"F0.wireOp",EDGE,"E1.2"),sQuery(id+"F0.wireOp",EDGE,"E1.3"),sQuery(id+"F0.wireOp",EDGE,"E1.4"),sQuery(id+"F0.wireOp",EDGE,"E1.5"),sQuery(id+"F0.wireOp",EDGE,"E1.6")])],"isStart":false});
            var sketch = newSketch(context, id + "F52", { "sketchPlane" : qUnion([Q0])});
            skText(sketch, "E21", { "text": "R", "fontName": "OpenSans-Regular.ttf"});
            skLineSegment(sketch, "E22", {"start": v(29.35, 27.92) * mm, "end": v(35.3, 32.67) * mm});
            skLineSegment(sketch, "E23", {"start": v(35.3, 32.67) * mm, "end": v(38.79, 28.3) * mm});
            skLineSegment(sketch, "E24", {"start": v(38.79, 28.3) * mm, "end": v(32.83, 23.55) * mm});
            skLineSegment(sketch, "E25", {"start": v(32.83, 23.55) * mm, "end": v(29.35, 27.92) * mm});
            skLineSegment(sketch, "E26", {"start": v(35.2, 30.74) * mm, "end": v(31.67, 27.92) * mm});
            skLineSegment(sketch, "E27", {"start": v(31.67, 27.92) * mm, "end": v(33.1, 26.13) * mm});
            skLineSegment(sketch, "E28", {"start": v(33.1, 26.13) * mm, "end": v(36.66, 28.98) * mm});
            skLineSegment(sketch, "E29", {"start": v(36.66, 28.98) * mm, "end": v(35.2, 30.74) * mm});
            skLineSegment(sketch, "E30", {"start": v(47.36, -8.09) * mm, "end": v(38.68, -6.17) * mm});
            skLineSegment(sketch, "E31", {"start": v(38.68, -6.17) * mm, "end": v(37.42, -11.88) * mm});
            skLineSegment(sketch, "E32", {"start": v(37.42, -11.88) * mm, "end": v(38.66, -12.15) * mm});
            skLineSegment(sketch, "E33", {"start": v(38.66, -12.15) * mm, "end": v(39.64, -7.69) * mm});
            skLineSegment(sketch, "E34", {"start": v(39.64, -7.69) * mm, "end": v(47.09, -9.33) * mm});
            skLineSegment(sketch, "E35", {"start": v(47.09, -9.33) * mm, "end": v(47.36, -8.09) * mm});
            skLineSegment(sketch, "E36", {"start": v(20.93, -34.05) * mm, "end": v(21.42, -42.93) * mm});
            skLineSegment(sketch, "E37", {"start": v(21.42, -42.93) * mm, "end": v(14.33, -37.57) * mm});
            skLineSegment(sketch, "E38", {"start": v(14.33, -37.57) * mm, "end": v(16.3, -36.62) * mm});
            skLineSegment(sketch, "E39", {"start": v(16.3, -36.62) * mm, "end": v(18.24, -38.25) * mm});
            skLineSegment(sketch, "E40", {"start": v(18.24, -38.25) * mm, "end": v(19.4, -37.65) * mm});
            skLineSegment(sketch, "E41", {"start": v(19.4, -37.65) * mm, "end": v(19.13, -35.12) * mm});
            skLineSegment(sketch, "E42", {"start": v(19.13, -35.12) * mm, "end": v(20.93, -34.05) * mm});
            skLineSegment(sketch, "E43", {"start": v(19.65, -38.65) * mm, "end": v(18.92, -39.03) * mm});
            skLineSegment(sketch, "E44", {"start": v(18.92, -39.03) * mm, "end": v(19.71, -39.66) * mm});
            skLineSegment(sketch, "E45", {"start": v(19.71, -39.66) * mm, "end": v(19.65, -38.65) * mm});
            skLineSegment(sketch, "E46", {"start": v(-15.7, -37.23) * mm, "end": v(-19.08, -44.06) * mm});
            skLineSegment(sketch, "E47", {"start": v(-19.08, -44.06) * mm, "end": v(-20.44, -43.38) * mm});
            skLineSegment(sketch, "E48", {"start": v(-20.44, -43.38) * mm, "end": v(-20.44, -39.06) * mm});
            skLineSegment(sketch, "E49", {"start": v(-20.44, -39.06) * mm, "end": v(-22.17, -42.46) * mm});
            skLineSegment(sketch, "E50", {"start": v(-22.17, -42.46) * mm, "end": v(-23.3, -41.88) * mm});
            skLineSegment(sketch, "E51", {"start": v(-23.3, -41.88) * mm, "end": v(-19.84, -35.1) * mm});
            skLineSegment(sketch, "E52", {"start": v(-19.84, -35.1) * mm, "end": v(-18.71, -35.67) * mm});
            skLineSegment(sketch, "E53", {"start": v(-18.71, -35.67) * mm, "end": v(-19.17, -41.5) * mm});
            skLineSegment(sketch, "E54", {"start": v(-19.17, -41.5) * mm, "end": v(-16.84, -36.7) * mm});
            skLineSegment(sketch, "E55", {"start": v(-16.84, -36.7) * mm, "end": v(-15.7, -37.23) * mm});
            skLineSegment(sketch, "E56", {"start": v(-38.7, -11.78) * mm, "end": v(-46.14, -13.44) * mm});
            skLineSegment(sketch, "E57", {"start": v(-46.14, -13.44) * mm, "end": v(-46.7, -10.96) * mm});
            skLineSegment(sketch, "E58", {"start": v(-38.7, -11.78) * mm, "end": v(-39.25, -9.3) * mm});
            skLineSegment(sketch, "E59", {"start": v(-46.7, -10.96) * mm, "end": v(-45.73, -10.13) * mm});
            skLineSegment(sketch, "E60", {"start": v(-45.73, -10.13) * mm, "end": v(-40.48, -8.96) * mm});
            skLineSegment(sketch, "E61", {"start": v(-40.48, -8.96) * mm, "end": v(-39.25, -9.3) * mm});
            skLineSegment(sketch, "E62", {"start": v(-45.47, -12.63) * mm, "end": v(-40.02, -11.38) * mm});
            skLineSegment(sketch, "E63", {"start": v(-40.02, -11.38) * mm, "end": v(-40.25, -10.39) * mm});
            skLineSegment(sketch, "E64", {"start": v(-40.25, -10.39) * mm, "end": v(-40.83, -9.9) * mm});
            skLineSegment(sketch, "E65", {"start": v(-45.47, -12.63) * mm, "end": v(-45.7, -11.64) * mm});
            skLineSegment(sketch, "E66", {"start": v(-45.7, -11.64) * mm, "end": v(-45.47, -10.91) * mm});
            skLineSegment(sketch, "E67", {"start": v(-45.47, -10.91) * mm, "end": v(-40.83, -9.9) * mm});
            skLineSegment(sketch, "E68", {"start": v(-33, 23.33) * mm, "end": v(-38.89, 28.18) * mm});
            skLineSegment(sketch, "E69", {"start": v(-38.89, 28.18) * mm, "end": v(-35.33, 32.49) * mm});
            skLineSegment(sketch, "E70", {"start": v(-35.33, 32.49) * mm, "end": v(-29.45, 27.64) * mm});
            skLineSegment(sketch, "E71", {"start": v(-29.45, 27.64) * mm, "end": v(-33, 23.33) * mm});
            skLineSegment(sketch, "E72", {"start": v(-36.6, 28.23) * mm, "end": v(-33.01, 25.34) * mm});
            skLineSegment(sketch, "E73", {"start": v(-33.01, 25.34) * mm, "end": v(-31.58, 27.12) * mm});
            skLineSegment(sketch, "E74", {"start": v(-31.58, 27.12) * mm, "end": v(-35.13, 29.99) * mm});
            skLineSegment(sketch, "E75", {"start": v(-35.13, 29.99) * mm, "end": v(-36.6, 28.23) * mm});
            const initialGuessF52  = {"E21": [-0.00332, 0.04047, 1, 0, 0.0075]};
            skSetInitialGuess(sketch, initialGuessF52);
            skSolve(sketch);
        }
        {
            var Q0;
            Q0=makeQuery(id+"F52.imprint","IMPRINT",FACE,{"disambiguationData":[TD([[makeQuery(id+"F52.imprint","IMPRINT",EDGE,{"derivedFrom":sQuery(id+"F52.wireOp",EDGE,"E21.sketch_text.stroke-0")}),-1.0]])]});
            var Q1;
            Q1=makeQuery(id+"F52.imprint","IMPRINT",FACE,{"disambiguationData":[TD([[makeQuery(id+"F52.imprint","IMPRINT",EDGE,{"derivedFrom":sQuery(id+"F52.wireOp",EDGE,"E68")}),-1.0]])]});
            var Q2;
            Q2=makeQuery(id+"F52.imprint","IMPRINT",FACE,{"disambiguationData":[TD([[makeQuery(id+"F52.imprint","IMPRINT",EDGE,{"derivedFrom":sQuery(id+"F52.wireOp",EDGE,"E22")}),-1.0]])]});
            var Q3;
            Q3=makeQuery(id+"F52.imprint","IMPRINT",FACE,{"disambiguationData":[TD([[makeQuery(id+"F52.imprint","IMPRINT",EDGE,{"derivedFrom":sQuery(id+"F52.wireOp",EDGE,"E30")}),1.0]])]});
            var Q4;
            Q4=makeQuery(id+"F52.imprint","IMPRINT",FACE,{"disambiguationData":[TD([[makeQuery(id+"F52.imprint","IMPRINT",EDGE,{"derivedFrom":sQuery(id+"F52.wireOp",EDGE,"E36")}),-1.0]])]});
            var Q5;
            Q5=makeQuery(id+"F52.imprint","IMPRINT",FACE,{"disambiguationData":[TD([[makeQuery(id+"F52.imprint","IMPRINT",EDGE,{"derivedFrom":sQuery(id+"F52.wireOp",EDGE,"E46")}),-1.0]])]});
            var Q6;
            Q6=makeQuery(id+"F52.imprint","IMPRINT",FACE,{"disambiguationData":[TD([[makeQuery(id+"F52.imprint","IMPRINT",EDGE,{"derivedFrom":sQuery(id+"F52.wireOp",EDGE,"E56")}),-1.0]])]});
            extrude(context, id + "F53", {"entities" : qUnion([Q0, Q1, Q2, Q3, Q4, Q5, Q6]), "operationType" : NewBodyOperationType.ADD, "depth" : 2.54 * mm, "offsetDistance" : 25.4 * mm});
        }
    });
